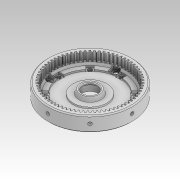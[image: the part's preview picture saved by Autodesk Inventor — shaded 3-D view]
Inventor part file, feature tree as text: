
AUTODESK INVENTOR PART (.ipt)
format: ipt  version: 2022 (Build 260153000, 153)  size: 1,792,000 bytes
history: native  units: mm
features: other x9, extrude x6, sketch x5, pattern_circular x4, chamfer x3, revolve x2, fillet x1, imported_body x1, projected_geometry x1
ambient origin geometry x8: Origin, YZ Plane, XZ Plane, XY Plane, X Axis, Y Axis, Z Axis, Center Point
bodies: Solid1 (feature_tree)
feature tree (32):
  other  "HD_mastersketch.ipt"
  other  "Blocks"
  revolve  "Revolution1"  [1 undecoded]
  extrude  "Extrusion1"  Depth=3.9mm
  extrude  "Extrusion3"  Depth=80.0mm TaperAngle=360.0deg
  pattern_circular  "Circular Pattern1"  [2 undecoded]
  extrude  "Extrusion2"  Depth=1.5mm
  fillet  "Fillet1"  Radius=700.0mm
  pattern_circular  "Circular Pattern2"  [2 undecoded]
  extrude  "Extrusion5"  Depth=1.5mm TaperAngle=0.0deg
  extrude  "Extrusion7"  Depth=1.5mm
  chamfer  "Chamfer1"  Distance=4.3mm
  extrude  "Extrusion8"  TaperAngle=0.0deg  [1 undecoded]
  chamfer  "Chamfer2"  Distance=2.268928mm
  pattern_circular  "Circular Pattern3"  [2 undecoded]
  revolve  "Revolution2"  [1 undecoded]
  pattern_circular  "Circular Pattern4"  Angle=45.0deg  [1 undecoded]
  chamfer  "Chamfer3"  Distance=8.726646mm
  other  "608 bearing"
  other  "Belt"
  other  "Rotor"
  imported_body  "Base"
  sketch  "Sketch5"  dims[d0=10.0mm d24=7.0mm d25=22.0mm d26=8.0mm]
  other  "M3NutDepth_bot"
  projected_geometry  "Projected Loop1"
  sketch  "Sketch7"  dims[d1=90.0deg d2=3.9mm]
  other  "BeltCutDepth_bot"
  sketch  "Sketch12"  dims[d4=4.0mm d5=0.0mm d6=80.0mm d7=360.0deg]
  sketch  "Sketch13"  dims[d9=0.8mm]
  sketch  "Sketch14"  dims[d11=1.8mm d12=4.0mm d13=0.0mm d14=0.45mm d15=700.0mm d16=360.0deg d18=5.7mm d19=4.0mm d20=0.0mm d29=47.0mm d30=4.3mm d31=0.0mm d32=0.0mm d38=2.268928mm d39=7.2mm d40=1.5mm d41=3.2mm d42=0.0mm d43=0.0mm d44=2.0mm d45=2.0mm d46=45.0deg d47=8.726646mm d48=0.523599mm d49=0.523599mm d50=0.523599mm d51=0.523599mm d52=0.523599mm d53=0.523599mm d56=2.792527mm d57=0.523599mm d58=68.0mm d59=70.740362mm d60=1.780032mm d61=9.749343mm d62=7.969311mm d63=6.189278mm d64=4.409246mm d65=2.629213mm d66=0.523599mm d67=0.523599mm d68=0.523599mm d69=0.523599mm d70=0.523599mm d72=11.529376mm d73=13.309408mm d74=15.089441mm d75=16.869473mm d76=18.649506mm d77=0.523599mm d78=0.523599mm d79=20.429538mm d80=22.209571mm d82=0.250579mm d83=72.932651mm d84=22.5mm d85=15.0mm d86=2.0mm d87=1.0mm d88=0.0mm d89=0.3mm d90=1.0mm d91=45.0deg d92=80.0mm d93=360.0deg d97=7.5mm d98=1.6mm d99=1.4mm d100=2.5mm d101=1.0mm d102=90.0deg d103=80.0mm d104=360.0deg d106=0.75mm d107=2.0mm d108=45.0deg]
  other  "608 bearing:1"
  other  "608 bearing:2"
note: 10 required parameter values undecoded (feature->parameter linkage not recoverable at this tier; creation-order binding heuristic only, values carry confidence <= 0.55)